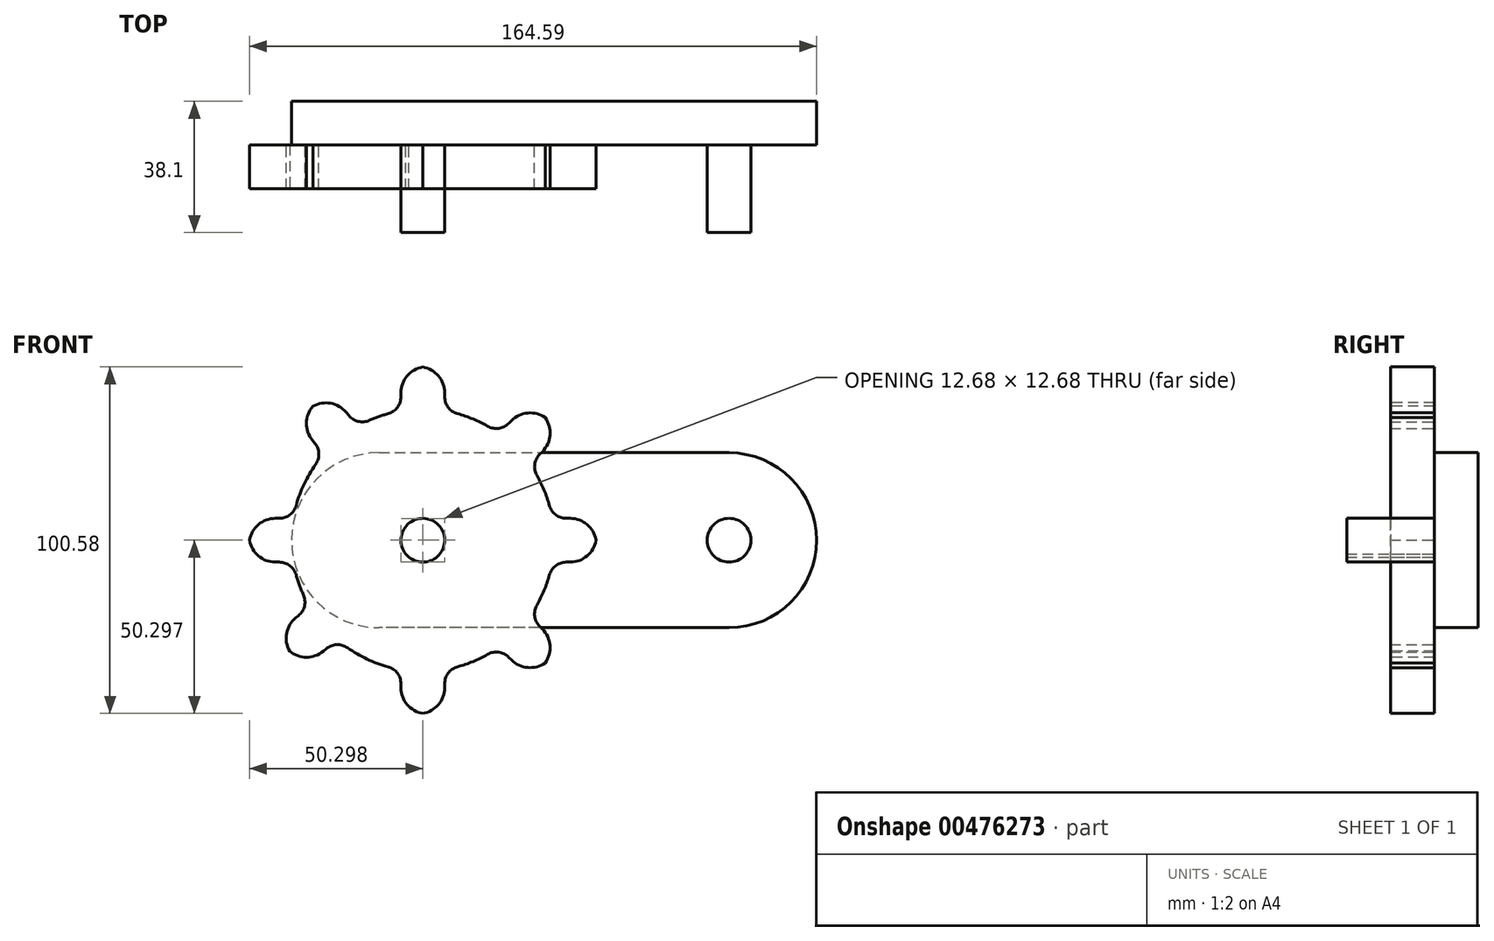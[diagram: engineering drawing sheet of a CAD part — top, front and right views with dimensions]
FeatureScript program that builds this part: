
annotation { "Feature Type Name" : "Feature", "Feature Type Description" : "" }
export const myFeature = defineFeature(function(context is Context, id is Id, definition is map)
    precondition{}
    {
        {
            var Q0;
            Q0=qCreatedBy(makeId("Front.planeOp"),FACE);
            var sketch = newSketch(context, id + "F0", { "sketchPlane" : qUnion([Q0])});
            skLineSegment(sketch, "E0.top", {"start": v(0, 25.4) * mm, "end": v(50.8, 25.4) * mm});
            skLineSegment(sketch, "E0.right", {"start": v(50.8, 0) * mm, "end": v(50.8, 25.4) * mm});
            skLineSegment(sketch, "E1.bottom", {"start": v(50.8, 25.4) * mm, "end": v(-50.8, 25.4) * mm});
            skLineSegment(sketch, "E1.top", {"start": v(50.8, -25.4) * mm, "end": v(-50.8, -25.4) * mm});
            skLineSegment(sketch, "E1.left", {"start": v(50.8, 25.4) * mm, "end": v(50.8, -25.4) * mm});
            skLineSegment(sketch, "E1.right", {"start": v(-50.8, 25.4) * mm, "end": v(-50.8, -25.4) * mm});
            skCircle(sketch, "E2", {"center": v(-50.8, 0) * mm, "radius": 25.4 * mm});
            skCircle(sketch, "E3", {"center": v(50.8, 0) * mm, "radius": 25.4 * mm});
            skSolve(sketch);
        }
        {
            var Q0;
            Q0 = qSketchRegion(id + "F0", true);
            extrude(context, id + "F1", {"entities" : qUnion([Q0]), "depth" : 12.7 * mm});
        }
        {
            var Q0;
            Q0=makeQuery(id+"F1.opExtrude","CAP_FACE",FACE,{"disambiguationData":[OSD([sQuery(id+"F0.wireOp",EDGE,"E1.bottom"),sQuery(id+"F0.wireOp",EDGE,"E1.top"),sQuery(id+"F0.wireOp",EDGE,"E2"),sQuery(id+"F0.wireOp",EDGE,"E3")])],"isStart":false});
            var sketch = newSketch(context, id + "F2", { "sketchPlane" : qUnion([Q0])});
            skCircle(sketch, "E4", {"center": v(50.8, 0) * mm, "radius": 50.8 * mm, "construction": true});
            skCircle(sketch, "E5", {"center": v(-38.1, 0) * mm, "radius": 38.1 * mm});
            skCircle(sketch, "E6", {"center": v(-38.1, 0) * mm, "radius": 6.35 * mm});
            skCircle(sketch, "E7", {"center": v(50.8, 0) * mm, "radius": 6.35 * mm});
            skCircle(sketch, "E8", {"center": v(-38.1, 0) * mm, "radius": 50.8 * mm, "construction": true});
            skCircle(sketch, "E9", {"center": v(50.8, 0) * mm, "radius": 38.1 * mm, "construction": true});
            skLineSegment(sketch, "E10.bottom", {"start": v(-44.45, 0) * mm, "end": v(-31.75, 0) * mm});
            skLineSegment(sketch, "E10.top", {"start": v(-44.45, -50.4) * mm, "end": v(-31.75, -50.4) * mm});
            skLineSegment(sketch, "E10.left", {"start": v(-44.45, 0) * mm, "end": v(-44.45, -50.4) * mm});
            skLineSegment(sketch, "E10.right", {"start": v(-31.75, 0) * mm, "end": v(-31.75, -50.4) * mm});
            skLineSegment(sketch, "E11.top", {"start": v(-44.45, 50.4) * mm, "end": v(-31.75, 50.4) * mm});
            skLineSegment(sketch, "E11.left", {"start": v(-44.45, 0) * mm, "end": v(-44.45, 50.4) * mm});
            skLineSegment(sketch, "E11.right", {"start": v(-31.75, 0) * mm, "end": v(-31.75, 50.4) * mm});
            skLineSegment(sketch, "E12.bottom", {"start": v(-38.1, 6.35) * mm, "end": v(12.3, 6.35) * mm});
            skLineSegment(sketch, "E12.top", {"start": v(-38.1, -6.35) * mm, "end": v(12.3, -6.35) * mm});
            skLineSegment(sketch, "E12.left", {"start": v(-38.1, 6.35) * mm, "end": v(-38.1, -6.35) * mm});
            skLineSegment(sketch, "E12.right", {"start": v(12.3, 6.35) * mm, "end": v(12.3, -6.35) * mm});
            skLineSegment(sketch, "E13", {"start": v(-6.95, 40.13) * mm, "end": v(-44.45, 2.63) * mm});
            skLineSegment(sketch, "E14", {"start": v(-6.95, 40.13) * mm, "end": v(2.03, 31.15) * mm});
            skLineSegment(sketch, "E15", {"start": v(2.03, 31.15) * mm, "end": v(-31.75, -2.63) * mm});
            skLineSegment(sketch, "E16", {"start": v(-65.16, 43) * mm, "end": v(-74.98, 34.94) * mm});
            skLineSegment(sketch, "E17", {"start": v(-74.98, 34.94) * mm, "end": v(-43, -4.03) * mm});
            skPoint(sketch, "E18.endSnap0", {"position": v(0, -25.4) * mm});
            skLineSegment(sketch, "E19", {"start": v(-65.16, 43) * mm, "end": v(-31.75, 2.27) * mm});
            skLineSegment(sketch, "E20", {"start": v(-38.1, 6.35) * mm, "end": v(-88.5, 6.35) * mm});
            skLineSegment(sketch, "E21", {"start": v(-88.5, 6.35) * mm, "end": v(-88.5, -6.35) * mm});
            skLineSegment(sketch, "E22", {"start": v(-88.5, -6.35) * mm, "end": v(-38.1, -6.35) * mm});
            skLineSegment(sketch, "E23", {"start": v(-72.82, -37.08) * mm, "end": v(-80.94, -27.3) * mm});
            skLineSegment(sketch, "E24", {"start": v(-72.82, -37.08) * mm, "end": v(-34.04, -4.89) * mm});
            skLineSegment(sketch, "E25", {"start": v(-80.94, -27.3) * mm, "end": v(-43.88, 2.63) * mm});
            skLineSegment(sketch, "E26", {"start": v(-6.98, -40.15) * mm, "end": v(2.01, -31.17) * mm});
            skLineSegment(sketch, "E27", {"start": v(-33.2, 4.03) * mm, "end": v(2.01, -31.17) * mm});
            skLineSegment(sketch, "E28", {"start": v(-6.98, -40.15) * mm, "end": v(-43, -4.03) * mm});
            skSolve(sketch);
        }
        {
            var Q0;
            {var subQ1=sQuery(id+"F2.wireOp",EDGE,"E6");var subQ3=makeQuery(id+"F2.imprint","INTERSECT",VERTEX,{"derivedFrom":[subQ1,sQuery(id+"F2.wireOp",EDGE,"E13")]});Q0=makeQuery(id+"F2.imprint","IMPRINT",FACE,{"disambiguationData":[TD([[makeQuery(id+"F2.imprint","IMPRINT",EDGE,{"disambiguationData":[TD([[subQ3,1.0]])],"derivedFrom":subQ1}),1.0]])]});}
            var Q1;
            {var subQ1=sQuery(id+"F2.wireOp",EDGE,"E6");var subQ3=makeQuery(id+"F2.imprint","INTERSECT",VERTEX,{"derivedFrom":[subQ1,sQuery(id+"F2.wireOp",EDGE,"E19")]});Q1=makeQuery(id+"F2.imprint","IMPRINT",FACE,{"disambiguationData":[TD([[makeQuery(id+"F2.imprint","IMPRINT",EDGE,{"disambiguationData":[TD([[subQ3,1.0]])],"derivedFrom":subQ1}),1.0]])]});}
            var Q2;
            {var subQ1=sQuery(id+"F2.wireOp",EDGE,"E6");var subQ5=sQuery(id+"F2.wireOp",EDGE,"LzmBPBVv-P9NO-bYiu-9SXB-eBMxNvQNguUM");var subQ6=makeQuery(id+"F2.imprint","INTERSECT",VERTEX,{"disambiguationData":[OD(0.0)],"derivedFrom":[subQ1,subQ5]});Q2=makeQuery(id+"F2.imprint","IMPRINT",FACE,{"disambiguationData":[TD([[makeQuery(id+"F2.imprint","IMPRINT",EDGE,{"disambiguationData":[TD([[subQ6,-1.0]])],"derivedFrom":subQ5}),1.0]])]});}
            var Q3;
            {var subQ1=sQuery(id+"F2.wireOp",EDGE,"E6");var subQ3=makeQuery(id+"F2.imprint","INTERSECT",VERTEX,{"derivedFrom":[subQ1,sQuery(id+"F2.wireOp",EDGE,"Yprd0iWj-599Q-bIJh-nxla-EBqFV5V5Is4s")]});Q3=makeQuery(id+"F2.imprint","IMPRINT",FACE,{"disambiguationData":[TD([[makeQuery(id+"F2.imprint","IMPRINT",EDGE,{"disambiguationData":[TD([[subQ3,1.0]])],"derivedFrom":subQ1}),1.0]])]});}
            var Q4;
            {var subQ1=sQuery(id+"F2.wireOp",EDGE,"E6");var subQ3=makeQuery(id+"F2.imprint","INTERSECT",VERTEX,{"derivedFrom":[subQ1,sQuery(id+"F2.wireOp",EDGE,"E24")]});Q4=makeQuery(id+"F2.imprint","IMPRINT",FACE,{"disambiguationData":[TD([[makeQuery(id+"F2.imprint","IMPRINT",EDGE,{"disambiguationData":[TD([[subQ3,1.0]])],"derivedFrom":subQ1}),1.0]])]});}
            var Q5;
            {var subQ1=sQuery(id+"F2.wireOp",EDGE,"E6");var subQ6=sQuery(id+"F2.wireOp",EDGE,"E28");var subQ7=makeQuery(id+"F2.imprint","INTERSECT",VERTEX,{"derivedFrom":[subQ1,subQ6]});Q5=makeQuery(id+"F2.imprint","IMPRINT",FACE,{"disambiguationData":[TD([[makeQuery(id+"F2.imprint","IMPRINT",EDGE,{"disambiguationData":[TD([[subQ7,-1.0]])],"derivedFrom":subQ6}),-1.0]])]});}
            extrude(context, id + "F3", {"entities" : qUnion([Q0, Q1, Q2, Q3, Q4, Q5]), "operationType" : NewBodyOperationType.ADD, "depth" : 25.4 * mm});
        }
        {
            var Q0;
            {var subQ5=sQuery(id+"F2.wireOp",EDGE,"E11.top");Q0=makeQuery(id+"F2.imprint","IMPRINT",FACE,{"disambiguationData":[TD([[makeQuery(id+"F2.imprint","IMPRINT",EDGE,{"derivedFrom":subQ5}),-1.0]])]});}
            var Q1;
            {var subQ0=sQuery(id+"F2.wireOp",EDGE,"E13");var subQ1=sQuery(id+"F2.wireOp",EDGE,"E5");var subQ2=makeQuery(id+"F2.imprint","INTERSECT",VERTEX,{"derivedFrom":[subQ1,subQ0]});Q1=makeQuery(id+"F2.imprint","IMPRINT",FACE,{"disambiguationData":[TD([[makeQuery(id+"F2.imprint","IMPRINT",EDGE,{"disambiguationData":[TD([[subQ2,-1.0]])],"derivedFrom":subQ1}),1.0]])]});}
            var Q2;
            {var subQ0=sQuery(id+"F2.wireOp",EDGE,"E20");var subQ1=sQuery(id+"F2.wireOp",EDGE,"E11.left");var subQ2=makeQuery(id+"F2.imprint","INTERSECT",VERTEX,{"derivedFrom":[subQ1,subQ0]});Q2=makeQuery(id+"F2.imprint","IMPRINT",FACE,{"disambiguationData":[TD([[makeQuery(id+"F2.imprint","IMPRINT",EDGE,{"disambiguationData":[TD([[subQ2,-1.0]])],"derivedFrom":subQ1}),-1.0]])]});}
            var Q3;
            {var subQ0=sQuery(id+"F2.wireOp",EDGE,"E19");var subQ1=sQuery(id+"F2.wireOp",EDGE,"E11.left");var subQ2=makeQuery(id+"F2.imprint","INTERSECT",VERTEX,{"derivedFrom":[subQ1,subQ0]});Q3=makeQuery(id+"F2.imprint","IMPRINT",FACE,{"disambiguationData":[TD([[makeQuery(id+"F2.imprint","IMPRINT",EDGE,{"disambiguationData":[TD([[subQ2,-1.0]])],"derivedFrom":subQ1}),1.0]])]});}
            var Q4;
            {var subQ5=sQuery(id+"F2.wireOp",EDGE,"E11.left");var subQ6=makeQuery(id+"F2.imprint","INTERSECT",VERTEX,{"derivedFrom":[subQ5,sQuery(id+"F2.wireOp",EDGE,"E13")]});Q4=makeQuery(id+"F2.imprint","IMPRINT",FACE,{"disambiguationData":[TD([[makeQuery(id+"F2.imprint","IMPRINT",EDGE,{"disambiguationData":[TD([[subQ6,1.0]])],"derivedFrom":subQ5}),1.0]])]});}
            var Q5;
            {var subQ0=sQuery(id+"F2.wireOp",EDGE,"E20");var subQ1=sQuery(id+"F2.wireOp",EDGE,"E17");var subQ2=makeQuery(id+"F2.imprint","INTERSECT",VERTEX,{"derivedFrom":[subQ1,subQ0]});Q5=makeQuery(id+"F2.imprint","IMPRINT",FACE,{"disambiguationData":[TD([[makeQuery(id+"F2.imprint","IMPRINT",EDGE,{"disambiguationData":[TD([[subQ2,1.0]])],"derivedFrom":subQ1}),-1.0]])]});}
            var Q6;
            {var subQ0=sQuery(id+"F2.wireOp",EDGE,"E12.bottom");var subQ1=sQuery(id+"F2.wireOp",EDGE,"E11.right");var subQ2=makeQuery(id+"F2.imprint","INTERSECT",VERTEX,{"derivedFrom":[subQ1,subQ0]});Q6=makeQuery(id+"F2.imprint","IMPRINT",FACE,{"disambiguationData":[TD([[makeQuery(id+"F2.imprint","IMPRINT",EDGE,{"disambiguationData":[TD([[subQ2,-1.0]])],"derivedFrom":subQ1}),1.0]])]});}
            var Q7;
            {var subQ5=sQuery(id+"F2.wireOp",EDGE,"E24");var subQ6=sQuery(id+"F2.wireOp",EDGE,"E5");var subQ7=makeQuery(id+"F2.imprint","INTERSECT",VERTEX,{"derivedFrom":[subQ6,subQ5]});Q7=makeQuery(id+"F2.imprint","IMPRINT",FACE,{"disambiguationData":[TD([[makeQuery(id+"F2.imprint","IMPRINT",EDGE,{"disambiguationData":[TD([[subQ7,-1.0]])],"derivedFrom":subQ6}),1.0]])]});}
            var Q8;
            {var subQ5=sQuery(id+"F2.wireOp",EDGE,"E17");var subQ7=sQuery(id+"F2.wireOp",EDGE,"E20");var subQ8=makeQuery(id+"F2.imprint","INTERSECT",VERTEX,{"derivedFrom":[subQ5,subQ7]});Q8=makeQuery(id+"F2.imprint","IMPRINT",FACE,{"disambiguationData":[TD([[makeQuery(id+"F2.imprint","IMPRINT",EDGE,{"disambiguationData":[TD([[subQ8,-1.0]])],"derivedFrom":subQ5}),-1.0]])]});}
            var Q9;
            {var subQ0=sQuery(id+"F2.wireOp",EDGE,"E10.right");var subQ1=sQuery(id+"F2.wireOp",EDGE,"E5");var subQ2=makeQuery(id+"F2.imprint","INTERSECT",VERTEX,{"derivedFrom":[subQ1,subQ0]});Q9=makeQuery(id+"F2.imprint","IMPRINT",FACE,{"disambiguationData":[TD([[makeQuery(id+"F2.imprint","IMPRINT",EDGE,{"disambiguationData":[TD([[subQ2,-1.0]])],"derivedFrom":subQ1}),1.0]])]});}
            var Q10;
            {var subQ0=sQuery(id+"F2.wireOp",EDGE,"E27");var subQ1=sQuery(id+"F2.wireOp",EDGE,"E5");var subQ2=makeQuery(id+"F2.imprint","INTERSECT",VERTEX,{"derivedFrom":[subQ1,subQ0]});Q10=makeQuery(id+"F2.imprint","IMPRINT",FACE,{"disambiguationData":[TD([[makeQuery(id+"F2.imprint","IMPRINT",EDGE,{"disambiguationData":[TD([[subQ2,1.0]])],"derivedFrom":subQ1}),-1.0]])]});}
            var Q11;
            {var subQ1=sQuery(id+"F2.wireOp",EDGE,"E14");Q11=makeQuery(id+"F2.imprint","IMPRINT",FACE,{"disambiguationData":[TD([[makeQuery(id+"F2.imprint","IMPRINT",EDGE,{"derivedFrom":subQ1}),-1.0]])]});}
            var Q12;
            {var subQ0=sQuery(id+"F2.wireOp",EDGE,"E13");var subQ1=sQuery(id+"F2.wireOp",EDGE,"E5");var subQ2=makeQuery(id+"F2.imprint","INTERSECT",VERTEX,{"derivedFrom":[subQ1,subQ0]});Q12=makeQuery(id+"F2.imprint","IMPRINT",FACE,{"disambiguationData":[TD([[makeQuery(id+"F2.imprint","IMPRINT",EDGE,{"disambiguationData":[TD([[subQ2,1.0]])],"derivedFrom":subQ1}),1.0]])]});}
            var Q13;
            {var subQ0=sQuery(id+"F2.wireOp",EDGE,"E22");var subQ1=sQuery(id+"F2.wireOp",EDGE,"E10.left");var subQ2=makeQuery(id+"F2.imprint","INTERSECT",VERTEX,{"derivedFrom":[subQ1,subQ0]});Q13=makeQuery(id+"F2.imprint","IMPRINT",FACE,{"disambiguationData":[TD([[makeQuery(id+"F2.imprint","IMPRINT",EDGE,{"disambiguationData":[TD([[subQ2,-1.0]])],"derivedFrom":subQ1}),1.0]])]});}
            var Q14;
            {var subQ0=sQuery(id+"F2.wireOp",EDGE,"E22");var subQ1=sQuery(id+"F2.wireOp",EDGE,"E5");var subQ2=makeQuery(id+"F2.imprint","INTERSECT",VERTEX,{"derivedFrom":[subQ1,subQ0]});Q14=makeQuery(id+"F2.imprint","IMPRINT",FACE,{"disambiguationData":[TD([[makeQuery(id+"F2.imprint","IMPRINT",EDGE,{"disambiguationData":[TD([[subQ2,-1.0]])],"derivedFrom":subQ1}),1.0]])]});}
            var Q15;
            {var subQ1=sQuery(id+"F2.wireOp",EDGE,"E22");var subQ6=sQuery(id+"F2.wireOp",EDGE,"E10.left");var subQ9=makeQuery(id+"F2.imprint","INTERSECT",VERTEX,{"derivedFrom":[subQ6,subQ1]});Q15=makeQuery(id+"F2.imprint","IMPRINT",FACE,{"disambiguationData":[TD([[makeQuery(id+"F2.imprint","IMPRINT",EDGE,{"disambiguationData":[TD([[subQ9,-1.0]])],"derivedFrom":subQ6}),-1.0]])]});}
            var Q16;
            {var subQ0=sQuery(id+"F2.wireOp",EDGE,"E27");var subQ1=sQuery(id+"F2.wireOp",EDGE,"E5");var subQ2=makeQuery(id+"F2.imprint","INTERSECT",VERTEX,{"derivedFrom":[subQ1,subQ0]});Q16=makeQuery(id+"F2.imprint","IMPRINT",FACE,{"disambiguationData":[TD([[makeQuery(id+"F2.imprint","IMPRINT",EDGE,{"disambiguationData":[TD([[subQ2,1.0]])],"derivedFrom":subQ1}),1.0]])]});}
            var Q17;
            {var subQ0=sQuery(id+"F2.wireOp",EDGE,"E21");Q17=makeQuery(id+"F2.imprint","IMPRINT",FACE,{"disambiguationData":[TD([[makeQuery(id+"F2.imprint","IMPRINT",EDGE,{"derivedFrom":subQ0}),1.0]])]});}
            var Q18;
            {var subQ5=sQuery(id+"F2.wireOp",EDGE,"E12.right");Q18=makeQuery(id+"F2.imprint","IMPRINT",FACE,{"disambiguationData":[TD([[makeQuery(id+"F2.imprint","IMPRINT",EDGE,{"derivedFrom":subQ5}),-1.0]])]});}
            var Q19;
            {var subQ1=sQuery(id+"F2.wireOp",EDGE,"E12.bottom");var subQ5=sQuery(id+"F2.wireOp",EDGE,"E5");var subQ6=makeQuery(id+"F2.imprint","INTERSECT",VERTEX,{"derivedFrom":[subQ5,subQ1]});Q19=makeQuery(id+"F2.imprint","IMPRINT",FACE,{"disambiguationData":[TD([[makeQuery(id+"F2.imprint","IMPRINT",EDGE,{"disambiguationData":[TD([[subQ6,1.0]])],"derivedFrom":subQ5}),1.0]])]});}
            var Q20;
            {var subQ0=sQuery(id+"F2.wireOp",EDGE,"E17");var subQ1=sQuery(id+"F2.wireOp",EDGE,"E10.left");var subQ2=makeQuery(id+"F2.imprint","INTERSECT",VERTEX,{"derivedFrom":[subQ1,subQ0]});Q20=makeQuery(id+"F2.imprint","IMPRINT",FACE,{"disambiguationData":[TD([[makeQuery(id+"F2.imprint","IMPRINT",EDGE,{"disambiguationData":[TD([[subQ2,-1.0]])],"derivedFrom":subQ1}),-1.0]])]});}
            var Q21;
            {var subQ3=sQuery(id+"F2.wireOp",EDGE,"E24");var subQ5=sQuery(id+"F2.wireOp",EDGE,"E10.left");var subQ6=makeQuery(id+"F2.imprint","INTERSECT",VERTEX,{"derivedFrom":[subQ5,subQ3]});Q21=makeQuery(id+"F2.imprint","IMPRINT",FACE,{"disambiguationData":[TD([[makeQuery(id+"F2.imprint","IMPRINT",EDGE,{"disambiguationData":[TD([[subQ6,-1.0]])],"derivedFrom":subQ5}),1.0]])]});}
            var Q22;
            {var subQ0=sQuery(id+"F2.wireOp",EDGE,"E27");var subQ1=sQuery(id+"F2.wireOp",EDGE,"E11.right");var subQ2=makeQuery(id+"F2.imprint","INTERSECT",VERTEX,{"derivedFrom":[subQ1,subQ0]});Q22=makeQuery(id+"F2.imprint","IMPRINT",FACE,{"disambiguationData":[TD([[makeQuery(id+"F2.imprint","IMPRINT",EDGE,{"disambiguationData":[TD([[subQ2,-1.0]])],"derivedFrom":subQ1}),-1.0]])]});}
            var Q23;
            {var subQ0=sQuery(id+"F2.wireOp",EDGE,"E11.left");var subQ1=sQuery(id+"F2.wireOp",EDGE,"E5");var subQ2=makeQuery(id+"F2.imprint","INTERSECT",VERTEX,{"derivedFrom":[subQ1,subQ0]});Q23=makeQuery(id+"F2.imprint","IMPRINT",FACE,{"disambiguationData":[TD([[makeQuery(id+"F2.imprint","IMPRINT",EDGE,{"disambiguationData":[TD([[subQ2,-1.0]])],"derivedFrom":subQ1}),1.0]])]});}
            var Q24;
            {var subQ0=sQuery(id+"F2.wireOp",EDGE,"E25");var subQ1=sQuery(id+"F2.wireOp",EDGE,"E5");var subQ2=makeQuery(id+"F2.imprint","INTERSECT",VERTEX,{"derivedFrom":[subQ1,subQ0]});Q24=makeQuery(id+"F2.imprint","IMPRINT",FACE,{"disambiguationData":[TD([[makeQuery(id+"F2.imprint","IMPRINT",EDGE,{"disambiguationData":[TD([[subQ2,-1.0]])],"derivedFrom":subQ1}),1.0]])]});}
            var Q25;
            {var subQ3=sQuery(id+"F2.wireOp",EDGE,"E19");var subQ5=sQuery(id+"F2.wireOp",EDGE,"E5");var subQ6=makeQuery(id+"F2.imprint","INTERSECT",VERTEX,{"derivedFrom":[subQ5,subQ3]});Q25=makeQuery(id+"F2.imprint","IMPRINT",FACE,{"disambiguationData":[TD([[makeQuery(id+"F2.imprint","IMPRINT",EDGE,{"disambiguationData":[TD([[subQ6,-1.0]])],"derivedFrom":subQ5}),1.0]])]});}
            var Q26;
            {var subQ0=sQuery(id+"F2.wireOp",EDGE,"E19");var subQ1=sQuery(id+"F2.wireOp",EDGE,"E11.left");var subQ2=makeQuery(id+"F2.imprint","INTERSECT",VERTEX,{"derivedFrom":[subQ1,subQ0]});Q26=makeQuery(id+"F2.imprint","IMPRINT",FACE,{"disambiguationData":[TD([[makeQuery(id+"F2.imprint","IMPRINT",EDGE,{"disambiguationData":[TD([[subQ2,-1.0]])],"derivedFrom":subQ1}),-1.0]])]});}
            var Q27;
            {var subQ0=sQuery(id+"F2.wireOp",EDGE,"E28");var subQ1=sQuery(id+"F2.wireOp",EDGE,"E5");var subQ2=makeQuery(id+"F2.imprint","INTERSECT",VERTEX,{"derivedFrom":[subQ1,subQ0]});Q27=makeQuery(id+"F2.imprint","IMPRINT",FACE,{"disambiguationData":[TD([[makeQuery(id+"F2.imprint","IMPRINT",EDGE,{"disambiguationData":[TD([[subQ2,-1.0]])],"derivedFrom":subQ1}),1.0]])]});}
            var Q28;
            {var subQ0=sQuery(id+"F2.wireOp",EDGE,"E15");var subQ1=sQuery(id+"F2.wireOp",EDGE,"E10.right");var subQ2=makeQuery(id+"F2.imprint","INTERSECT",VERTEX,{"derivedFrom":[subQ1,subQ0]});Q28=makeQuery(id+"F2.imprint","IMPRINT",FACE,{"disambiguationData":[TD([[makeQuery(id+"F2.imprint","IMPRINT",EDGE,{"disambiguationData":[TD([[subQ2,-1.0]])],"derivedFrom":subQ1}),1.0]])]});}
            var Q29;
            {var subQ0=sQuery(id+"F2.wireOp",EDGE,"E10.left");var subQ1=sQuery(id+"F2.wireOp",EDGE,"E5");var subQ2=makeQuery(id+"F2.imprint","INTERSECT",VERTEX,{"derivedFrom":[subQ1,subQ0]});Q29=makeQuery(id+"F2.imprint","IMPRINT",FACE,{"disambiguationData":[TD([[makeQuery(id+"F2.imprint","IMPRINT",EDGE,{"disambiguationData":[TD([[subQ2,-1.0]])],"derivedFrom":subQ1}),1.0]])]});}
            var Q30;
            {var subQ0=sQuery(id+"F2.wireOp",EDGE,"E17");var subQ1=sQuery(id+"F2.wireOp",EDGE,"E5");var subQ2=makeQuery(id+"F2.imprint","INTERSECT",VERTEX,{"derivedFrom":[subQ1,subQ0]});Q30=makeQuery(id+"F2.imprint","IMPRINT",FACE,{"disambiguationData":[TD([[makeQuery(id+"F2.imprint","IMPRINT",EDGE,{"disambiguationData":[TD([[subQ2,-1.0]])],"derivedFrom":subQ1}),1.0]])]});}
            var Q31;
            {var subQ0=sQuery(id+"F2.wireOp",EDGE,"E12.top");var subQ1=sQuery(id+"F2.wireOp",EDGE,"E10.right");var subQ2=makeQuery(id+"F2.imprint","INTERSECT",VERTEX,{"derivedFrom":[subQ1,subQ0]});Q31=makeQuery(id+"F2.imprint","IMPRINT",FACE,{"disambiguationData":[TD([[makeQuery(id+"F2.imprint","IMPRINT",EDGE,{"disambiguationData":[TD([[subQ2,-1.0]])],"derivedFrom":subQ1}),-1.0]])]});}
            var Q32;
            {var subQ0=sQuery(id+"F2.wireOp",EDGE,"E13");var subQ1=sQuery(id+"F2.wireOp",EDGE,"E11.right");var subQ2=makeQuery(id+"F2.imprint","INTERSECT",VERTEX,{"derivedFrom":[subQ1,subQ0]});Q32=makeQuery(id+"F2.imprint","IMPRINT",FACE,{"disambiguationData":[TD([[makeQuery(id+"F2.imprint","IMPRINT",EDGE,{"disambiguationData":[TD([[subQ2,-1.0]])],"derivedFrom":subQ1}),-1.0]])]});}
            var Q33;
            {var subQ0=sQuery(id+"F2.wireOp",EDGE,"E28");var subQ1=sQuery(id+"F2.wireOp",EDGE,"E10.right");var subQ2=makeQuery(id+"F2.imprint","INTERSECT",VERTEX,{"derivedFrom":[subQ1,subQ0]});Q33=makeQuery(id+"F2.imprint","IMPRINT",FACE,{"disambiguationData":[TD([[makeQuery(id+"F2.imprint","IMPRINT",EDGE,{"disambiguationData":[TD([[subQ2,-1.0]])],"derivedFrom":subQ1}),1.0]])]});}
            var Q34;
            {var subQ0=sQuery(id+"F2.wireOp",EDGE,"E15");var subQ1=sQuery(id+"F2.wireOp",EDGE,"E5");var subQ2=makeQuery(id+"F2.imprint","INTERSECT",VERTEX,{"derivedFrom":[subQ1,subQ0]});Q34=makeQuery(id+"F2.imprint","IMPRINT",FACE,{"disambiguationData":[TD([[makeQuery(id+"F2.imprint","IMPRINT",EDGE,{"disambiguationData":[TD([[subQ2,-1.0]])],"derivedFrom":subQ1}),-1.0]])]});}
            var Q35;
            {var subQ0=sQuery(id+"F2.wireOp",EDGE,"E20");var subQ1=sQuery(id+"F2.wireOp",EDGE,"E11.left");var subQ2=makeQuery(id+"F2.imprint","INTERSECT",VERTEX,{"derivedFrom":[subQ1,subQ0]});Q35=makeQuery(id+"F2.imprint","IMPRINT",FACE,{"disambiguationData":[TD([[makeQuery(id+"F2.imprint","IMPRINT",EDGE,{"disambiguationData":[TD([[subQ2,-1.0]])],"derivedFrom":subQ1}),1.0]])]});}
            var Q36;
            {var subQ5=sQuery(id+"F2.wireOp",EDGE,"E16");Q36=makeQuery(id+"F2.imprint","IMPRINT",FACE,{"disambiguationData":[TD([[makeQuery(id+"F2.imprint","IMPRINT",EDGE,{"derivedFrom":subQ5}),1.0]])]});}
            var Q37;
            {var subQ7=sQuery(id+"F2.wireOp",EDGE,"E15");var subQ9=sQuery(id+"F2.wireOp",EDGE,"E5");var subQ10=makeQuery(id+"F2.imprint","INTERSECT",VERTEX,{"derivedFrom":[subQ9,subQ7]});Q37=makeQuery(id+"F2.imprint","IMPRINT",FACE,{"disambiguationData":[TD([[makeQuery(id+"F2.imprint","IMPRINT",EDGE,{"disambiguationData":[TD([[subQ10,-1.0]])],"derivedFrom":subQ9}),1.0]])]});}
            var Q38;
            {var subQ0=sQuery(id+"F2.wireOp",EDGE,"E11.right");var subQ1=sQuery(id+"F2.wireOp",EDGE,"E5");var subQ2=makeQuery(id+"F2.imprint","INTERSECT",VERTEX,{"derivedFrom":[subQ1,subQ0]});Q38=makeQuery(id+"F2.imprint","IMPRINT",FACE,{"disambiguationData":[TD([[makeQuery(id+"F2.imprint","IMPRINT",EDGE,{"disambiguationData":[TD([[subQ2,-1.0]])],"derivedFrom":subQ1}),1.0]])]});}
            var Q39;
            {var subQ0=sQuery(id+"F2.wireOp",EDGE,"E24");var subQ1=sQuery(id+"F2.wireOp",EDGE,"E10.left");var subQ2=makeQuery(id+"F2.imprint","INTERSECT",VERTEX,{"derivedFrom":[subQ1,subQ0]});Q39=makeQuery(id+"F2.imprint","IMPRINT",FACE,{"disambiguationData":[TD([[makeQuery(id+"F2.imprint","IMPRINT",EDGE,{"disambiguationData":[TD([[subQ2,-1.0]])],"derivedFrom":subQ1}),-1.0]])]});}
            var Q40;
            {var subQ1=sQuery(id+"F2.wireOp",EDGE,"E26");Q40=makeQuery(id+"F2.imprint","IMPRINT",FACE,{"disambiguationData":[TD([[makeQuery(id+"F2.imprint","IMPRINT",EDGE,{"derivedFrom":subQ1}),1.0]])]});}
            var Q41;
            {var subQ0=sQuery(id+"F2.wireOp",EDGE,"E25");var subQ1=sQuery(id+"F2.wireOp",EDGE,"E22");var subQ2=makeQuery(id+"F2.imprint","INTERSECT",VERTEX,{"derivedFrom":[subQ1,subQ0]});Q41=makeQuery(id+"F2.imprint","IMPRINT",FACE,{"disambiguationData":[TD([[makeQuery(id+"F2.imprint","IMPRINT",EDGE,{"disambiguationData":[TD([[subQ2,1.0]])],"derivedFrom":subQ1}),-1.0]])]});}
            var Q42;
            {var subQ0=sQuery(id+"F2.wireOp",EDGE,"E15");var subQ1=sQuery(id+"F2.wireOp",EDGE,"E5");var subQ2=makeQuery(id+"F2.imprint","INTERSECT",VERTEX,{"derivedFrom":[subQ1,subQ0]});Q42=makeQuery(id+"F2.imprint","IMPRINT",FACE,{"disambiguationData":[TD([[makeQuery(id+"F2.imprint","IMPRINT",EDGE,{"disambiguationData":[TD([[subQ2,1.0]])],"derivedFrom":subQ1}),1.0]])]});}
            var Q43;
            {var subQ0=sQuery(id+"F2.wireOp",EDGE,"E27");var subQ1=sQuery(id+"F2.wireOp",EDGE,"E5");var subQ2=makeQuery(id+"F2.imprint","INTERSECT",VERTEX,{"derivedFrom":[subQ1,subQ0]});Q43=makeQuery(id+"F2.imprint","IMPRINT",FACE,{"disambiguationData":[TD([[makeQuery(id+"F2.imprint","IMPRINT",EDGE,{"disambiguationData":[TD([[subQ2,-1.0]])],"derivedFrom":subQ1}),1.0]])]});}
            var Q44;
            {var subQ5=sQuery(id+"F2.wireOp",EDGE,"E10.top");Q44=makeQuery(id+"F2.imprint","IMPRINT",FACE,{"disambiguationData":[TD([[makeQuery(id+"F2.imprint","IMPRINT",EDGE,{"derivedFrom":subQ5}),1.0]])]});}
            var Q45;
            {var subQ5=sQuery(id+"F2.wireOp",EDGE,"E23");Q45=makeQuery(id+"F2.imprint","IMPRINT",FACE,{"disambiguationData":[TD([[makeQuery(id+"F2.imprint","IMPRINT",EDGE,{"derivedFrom":subQ5}),-1.0]])]});}
            var Q46;
            {var subQ1=sQuery(id+"F2.wireOp",EDGE,"E10.left");var subQ5=sQuery(id+"F2.wireOp",EDGE,"E17");var subQ8=makeQuery(id+"F2.imprint","INTERSECT",VERTEX,{"derivedFrom":[subQ1,subQ5]});Q46=makeQuery(id+"F2.imprint","IMPRINT",FACE,{"disambiguationData":[TD([[makeQuery(id+"F2.imprint","IMPRINT",EDGE,{"disambiguationData":[TD([[subQ8,-1.0]])],"derivedFrom":subQ1}),1.0]])]});}
            var Q47;
            {var subQ0=sQuery(id+"F2.wireOp",EDGE,"E20");var subQ1=sQuery(id+"F2.wireOp",EDGE,"E5");var subQ2=makeQuery(id+"F2.imprint","INTERSECT",VERTEX,{"derivedFrom":[subQ1,subQ0]});Q47=makeQuery(id+"F2.imprint","IMPRINT",FACE,{"disambiguationData":[TD([[makeQuery(id+"F2.imprint","IMPRINT",EDGE,{"disambiguationData":[TD([[subQ2,-1.0]])],"derivedFrom":subQ1}),1.0]])]});}
            var Q48;
            {var subQ1=sQuery(id+"F2.wireOp",EDGE,"E10.right");var subQ7=makeQuery(id+"F2.imprint","INTERSECT",VERTEX,{"derivedFrom":[subQ1,sQuery(id+"F2.wireOp",EDGE,"E15")]});Q48=makeQuery(id+"F2.imprint","IMPRINT",FACE,{"disambiguationData":[TD([[makeQuery(id+"F2.imprint","IMPRINT",EDGE,{"disambiguationData":[TD([[subQ7,-1.0]])],"derivedFrom":subQ1}),-1.0]])]});}
            var Q49;
            {var subQ0=sQuery(id+"F2.wireOp",EDGE,"E27");var subQ1=sQuery(id+"F2.wireOp",EDGE,"E11.right");var subQ2=makeQuery(id+"F2.imprint","INTERSECT",VERTEX,{"derivedFrom":[subQ1,subQ0]});Q49=makeQuery(id+"F2.imprint","IMPRINT",FACE,{"disambiguationData":[TD([[makeQuery(id+"F2.imprint","IMPRINT",EDGE,{"disambiguationData":[TD([[subQ2,-1.0]])],"derivedFrom":subQ1}),1.0]])]});}
            var Q50;
            {var subQ0=sQuery(id+"F2.wireOp",EDGE,"E25");var subQ1=sQuery(id+"F2.wireOp",EDGE,"E6");var subQ2=makeQuery(id+"F2.imprint","INTERSECT",VERTEX,{"derivedFrom":[subQ1,subQ0]});Q50=makeQuery(id+"F2.imprint","IMPRINT",FACE,{"disambiguationData":[TD([[makeQuery(id+"F2.imprint","IMPRINT",EDGE,{"disambiguationData":[TD([[subQ2,1.0]])],"derivedFrom":subQ1}),-1.0]])]});}
            var Q51;
            {var subQ0=sQuery(id+"F2.wireOp",EDGE,"E13");var subQ1=sQuery(id+"F2.wireOp",EDGE,"E11.left");var subQ2=makeQuery(id+"F2.imprint","INTERSECT",VERTEX,{"derivedFrom":[subQ1,subQ0]});Q51=makeQuery(id+"F2.imprint","IMPRINT",FACE,{"disambiguationData":[TD([[makeQuery(id+"F2.imprint","IMPRINT",EDGE,{"disambiguationData":[TD([[subQ2,-1.0]])],"derivedFrom":subQ1}),-1.0]])]});}
            var Q52;
            {var subQ0=sQuery(id+"F2.wireOp",EDGE,"E12.bottom");var subQ3=sQuery(id+"F2.wireOp",EDGE,"E19");var subQ5=makeQuery(id+"F2.imprint","INTERSECT",VERTEX,{"derivedFrom":[subQ0,subQ3]});Q52=makeQuery(id+"F2.imprint","IMPRINT",FACE,{"disambiguationData":[TD([[makeQuery(id+"F2.imprint","IMPRINT",EDGE,{"disambiguationData":[TD([[subQ5,-1.0]])],"derivedFrom":subQ3}),-1.0]])]});}
            var Q53;
            {var subQ0=sQuery(id+"F2.wireOp",EDGE,"E22");var subQ1=sQuery(id+"F2.wireOp",EDGE,"E5");var subQ2=makeQuery(id+"F2.imprint","INTERSECT",VERTEX,{"derivedFrom":[subQ1,subQ0]});Q53=makeQuery(id+"F2.imprint","IMPRINT",FACE,{"disambiguationData":[TD([[makeQuery(id+"F2.imprint","IMPRINT",EDGE,{"disambiguationData":[TD([[subQ2,1.0]])],"derivedFrom":subQ1}),1.0]])]});}
            var Q54;
            {var subQ3=sQuery(id+"F2.wireOp",EDGE,"E19");var subQ5=sQuery(id+"F2.wireOp",EDGE,"E13");var subQ7=makeQuery(id+"F2.imprint","INTERSECT",VERTEX,{"derivedFrom":[subQ5,subQ3]});Q54=makeQuery(id+"F2.imprint","IMPRINT",FACE,{"disambiguationData":[TD([[makeQuery(id+"F2.imprint","IMPRINT",EDGE,{"disambiguationData":[TD([[subQ7,-1.0]])],"derivedFrom":subQ5}),1.0]])]});}
            var Q55;
            {var subQ5=sQuery(id+"F2.wireOp",EDGE,"E11.right");var subQ6=makeQuery(id+"F2.imprint","INTERSECT",VERTEX,{"derivedFrom":[subQ5,sQuery(id+"F2.wireOp",EDGE,"E19")]});Q55=makeQuery(id+"F2.imprint","IMPRINT",FACE,{"disambiguationData":[TD([[makeQuery(id+"F2.imprint","IMPRINT",EDGE,{"disambiguationData":[TD([[subQ6,-1.0]])],"derivedFrom":subQ5}),-1.0]])]});}
            var Q56;
            {var subQ0=sQuery(id+"F2.wireOp",EDGE,"E19");var subQ1=sQuery(id+"F2.wireOp",EDGE,"E11.right");var subQ2=makeQuery(id+"F2.imprint","INTERSECT",VERTEX,{"derivedFrom":[subQ1,subQ0]});Q56=makeQuery(id+"F2.imprint","IMPRINT",FACE,{"disambiguationData":[TD([[makeQuery(id+"F2.imprint","IMPRINT",EDGE,{"disambiguationData":[TD([[subQ2,-1.0]])],"derivedFrom":subQ1}),1.0]])]});}
            var Q57;
            {var subQ1=sQuery(id+"F2.wireOp",EDGE,"E6");var subQ3=sQuery(id+"F2.wireOp",EDGE,"E13");var subQ4=makeQuery(id+"F2.imprint","INTERSECT",VERTEX,{"derivedFrom":[subQ1,subQ3]});Q57=makeQuery(id+"F2.imprint","IMPRINT",FACE,{"disambiguationData":[TD([[makeQuery(id+"F2.imprint","IMPRINT",EDGE,{"disambiguationData":[TD([[subQ4,1.0]])],"derivedFrom":subQ3}),1.0]])]});}
            var Q58;
            {var subQ1=sQuery(id+"F2.wireOp",EDGE,"E6");var subQ3=sQuery(id+"F2.wireOp",EDGE,"E28");var subQ4=makeQuery(id+"F2.imprint","INTERSECT",VERTEX,{"derivedFrom":[subQ1,subQ3]});Q58=makeQuery(id+"F2.imprint","IMPRINT",FACE,{"disambiguationData":[TD([[makeQuery(id+"F2.imprint","IMPRINT",EDGE,{"disambiguationData":[TD([[subQ4,1.0]])],"derivedFrom":subQ3}),-1.0]])]});}
            var Q59;
            {var subQ1=sQuery(id+"F2.wireOp",EDGE,"E6");var subQ3=sQuery(id+"F2.wireOp",EDGE,"E24");var subQ4=makeQuery(id+"F2.imprint","INTERSECT",VERTEX,{"derivedFrom":[subQ1,subQ3]});Q59=makeQuery(id+"F2.imprint","IMPRINT",FACE,{"disambiguationData":[TD([[makeQuery(id+"F2.imprint","IMPRINT",EDGE,{"disambiguationData":[TD([[subQ4,1.0]])],"derivedFrom":subQ3}),1.0]])]});}
            var Q60;
            {var subQ0=sQuery(id+"F2.wireOp",EDGE,"E10.left");var subQ3=sQuery(id+"F2.wireOp",EDGE,"E17");var subQ5=makeQuery(id+"F2.imprint","INTERSECT",VERTEX,{"derivedFrom":[subQ0,subQ3]});Q60=makeQuery(id+"F2.imprint","IMPRINT",FACE,{"disambiguationData":[TD([[makeQuery(id+"F2.imprint","IMPRINT",EDGE,{"disambiguationData":[TD([[subQ5,-1.0]])],"derivedFrom":subQ3}),1.0]])]});}
            var Q61;
            {var subQ0=sQuery(id+"F2.wireOp",EDGE,"E11.right");var subQ3=sQuery(id+"F2.wireOp",EDGE,"E19");var subQ5=makeQuery(id+"F2.imprint","INTERSECT",VERTEX,{"derivedFrom":[subQ0,subQ3]});Q61=makeQuery(id+"F2.imprint","IMPRINT",FACE,{"disambiguationData":[TD([[makeQuery(id+"F2.imprint","IMPRINT",EDGE,{"disambiguationData":[TD([[subQ5,1.0]])],"derivedFrom":subQ3}),-1.0]])]});}
            var Q62;
            {var subQ0=sQuery(id+"F2.wireOp",EDGE,"E28");var subQ1=sQuery(id+"F2.wireOp",EDGE,"E6");var subQ3=makeQuery(id+"F2.imprint","INTERSECT",VERTEX,{"derivedFrom":[subQ1,subQ0]});Q62=makeQuery(id+"F2.imprint","IMPRINT",FACE,{"disambiguationData":[TD([[makeQuery(id+"F2.imprint","IMPRINT",EDGE,{"disambiguationData":[TD([[subQ3,1.0]])],"derivedFrom":subQ1}),1.0]])]});}
            var Q63;
            {var subQ1=sQuery(id+"F2.wireOp",EDGE,"E12.top");var subQ3=sQuery(id+"F2.wireOp",EDGE,"E24");var subQ4=makeQuery(id+"F2.imprint","INTERSECT",VERTEX,{"derivedFrom":[subQ1,subQ3]});Q63=makeQuery(id+"F2.imprint","IMPRINT",FACE,{"disambiguationData":[TD([[makeQuery(id+"F2.imprint","IMPRINT",EDGE,{"disambiguationData":[TD([[subQ4,1.0]])],"derivedFrom":subQ3}),1.0]])]});}
            var Q64;
            {var subQ1=sQuery(id+"F2.wireOp",EDGE,"E10.left");var subQ3=sQuery(id+"F2.wireOp",EDGE,"E17");var subQ4=makeQuery(id+"F2.imprint","INTERSECT",VERTEX,{"derivedFrom":[subQ1,subQ3]});Q64=makeQuery(id+"F2.imprint","IMPRINT",FACE,{"disambiguationData":[TD([[makeQuery(id+"F2.imprint","IMPRINT",EDGE,{"disambiguationData":[TD([[subQ4,1.0]])],"derivedFrom":subQ3}),1.0]])]});}
            var Q65;
            {var subQ1=sQuery(id+"F2.wireOp",EDGE,"E6");var subQ3=sQuery(id+"F2.wireOp",EDGE,"E25");var subQ4=makeQuery(id+"F2.imprint","INTERSECT",VERTEX,{"derivedFrom":[subQ1,subQ3]});Q65=makeQuery(id+"F2.imprint","IMPRINT",FACE,{"disambiguationData":[TD([[makeQuery(id+"F2.imprint","IMPRINT",EDGE,{"disambiguationData":[TD([[subQ4,1.0]])],"derivedFrom":subQ3}),-1.0]])]});}
            extrude(context, id + "F4", {"entities" : qUnion([Q0, Q1, Q2, Q3, Q4, Q5, Q6, Q7, Q8, Q9, Q10, Q11, Q12, Q13, Q14, Q15, Q16, Q17, Q18, Q19, Q20, Q21, Q22, Q23, Q24, Q25, Q26, Q27, Q28, Q29, Q30, Q31, Q32, Q33, Q34, Q35, Q36, Q37, Q38, Q39, Q40, Q41, Q42, Q43, Q44, Q45, Q46, Q47, Q48, Q49, Q50, Q51, Q52, Q53, Q54, Q55, Q56, Q57, Q58, Q59, Q60, Q61, Q62, Q63, Q64, Q65]), "depth" : 12.7 * mm});
        }
        {
            var Q0;
            Q0=makeQuery(id+"F4.opExtrude","SWEPT_EDGE",EDGE,{"disambiguationData":[OSD([sQuery(id+"F2.wireOp",EDGE,"E16"),sQuery(id+"F2.wireOp",EDGE,"E19")])]});
            var Q1;
            Q1=makeQuery(id+"F4.opExtrude","SWEPT_EDGE",EDGE,{"disambiguationData":[OSD([sQuery(id+"F2.wireOp",EDGE,"E16"),sQuery(id+"F2.wireOp",EDGE,"E17")])]});
            var Q2;
            Q2=makeQuery(id+"F4.opExtrude","SWEPT_EDGE",EDGE,{"disambiguationData":[OSD([sQuery(id+"F2.wireOp",EDGE,"E11.top"),sQuery(id+"F2.wireOp",EDGE,"E11.left")])]});
            var Q3;
            Q3=makeQuery(id+"F4.opExtrude","SWEPT_EDGE",EDGE,{"disambiguationData":[OSD([sQuery(id+"F2.wireOp",EDGE,"E11.top"),sQuery(id+"F2.wireOp",EDGE,"E11.right")])]});
            var Q4;
            Q4=makeQuery(id+"F4.opExtrude","SWEPT_EDGE",EDGE,{"disambiguationData":[OSD([sQuery(id+"F2.wireOp",EDGE,"E13"),sQuery(id+"F2.wireOp",EDGE,"E14")])]});
            var Q5;
            Q5=makeQuery(id+"F4.opExtrude","SWEPT_EDGE",EDGE,{"disambiguationData":[OSD([sQuery(id+"F2.wireOp",EDGE,"E14"),sQuery(id+"F2.wireOp",EDGE,"E15")])]});
            var Q6;
            Q6=makeQuery(id+"F4.opExtrude","SWEPT_EDGE",EDGE,{"disambiguationData":[OSD([sQuery(id+"F2.wireOp",EDGE,"E12.bottom"),sQuery(id+"F2.wireOp",EDGE,"E12.right")])]});
            var Q7;
            Q7=makeQuery(id+"F4.opExtrude","SWEPT_EDGE",EDGE,{"disambiguationData":[OSD([sQuery(id+"F2.wireOp",EDGE,"E12.top"),sQuery(id+"F2.wireOp",EDGE,"E12.right")])]});
            var Q8;
            Q8=makeQuery(id+"F4.opExtrude","SWEPT_EDGE",EDGE,{"disambiguationData":[OSD([sQuery(id+"F2.wireOp",EDGE,"E26"),sQuery(id+"F2.wireOp",EDGE,"E28")])]});
            var Q9;
            Q9=makeQuery(id+"F4.opExtrude","SWEPT_EDGE",EDGE,{"disambiguationData":[OSD([sQuery(id+"F2.wireOp",EDGE,"E26"),sQuery(id+"F2.wireOp",EDGE,"E27")])]});
            var Q10;
            Q10=makeQuery(id+"F4.opExtrude","SWEPT_EDGE",EDGE,{"disambiguationData":[OSD([sQuery(id+"F2.wireOp",EDGE,"E10.top"),sQuery(id+"F2.wireOp",EDGE,"E10.right")])]});
            var Q11;
            Q11=makeQuery(id+"F4.opExtrude","SWEPT_EDGE",EDGE,{"disambiguationData":[OSD([sQuery(id+"F2.wireOp",EDGE,"E10.top"),sQuery(id+"F2.wireOp",EDGE,"E10.left")])]});
            var Q12;
            Q12=makeQuery(id+"F4.opExtrude","SWEPT_EDGE",EDGE,{"disambiguationData":[OSD([sQuery(id+"F2.wireOp",EDGE,"E23"),sQuery(id+"F2.wireOp",EDGE,"E24")])]});
            var Q13;
            Q13=makeQuery(id+"F4.opExtrude","SWEPT_EDGE",EDGE,{"disambiguationData":[OSD([sQuery(id+"F2.wireOp",EDGE,"E23"),sQuery(id+"F2.wireOp",EDGE,"E25")])]});
            var Q14;
            Q14=makeQuery(id+"F4.opExtrude","SWEPT_EDGE",EDGE,{"disambiguationData":[OSD([sQuery(id+"F2.wireOp",EDGE,"E21"),sQuery(id+"F2.wireOp",EDGE,"E22")])]});
            var Q15;
            Q15=makeQuery(id+"F4.opExtrude","SWEPT_EDGE",EDGE,{"disambiguationData":[OSD([sQuery(id+"F2.wireOp",EDGE,"E20"),sQuery(id+"F2.wireOp",EDGE,"E21")])]});
            fillet(context, id + "F5", {"entities" : qUnion([Q0, Q1, Q2, Q3, Q4, Q5, Q6, Q7, Q8, Q9, Q10, Q11, Q12, Q13, Q14, Q15]), "radius" : 7.62 * mm, "tangentPropagation" : true, "allowEdgeOverflow" : false});
        }
        {
            var Q0;
            Q0=makeQuery(id+"F2.imprint","IMPRINT",FACE,{"disambiguationData":[TD([[makeQuery(id+"F2.imprint","IMPRINT",EDGE,{"derivedFrom":sQuery(id+"F2.wireOp",EDGE,"E7")}),1.0]])]});
            extrude(context, id + "F6", {"entities" : qUnion([Q0]), "operationType" : NewBodyOperationType.ADD, "depth" : 25.4 * mm});
        }
        {
            var Q0;
            Q0=makeQuery(id+"F4.opExtrude","SWEPT_EDGE",EDGE,{"disambiguationData":[OSD([sQuery(id+"F2.wireOp",EDGE,"E5"),sQuery(id+"F2.wireOp",EDGE,"E11.right")])]});
            var Q1;
            Q1=makeQuery(id+"F4.opExtrude","SWEPT_EDGE",EDGE,{"disambiguationData":[OSD([sQuery(id+"F2.wireOp",EDGE,"E5"),sQuery(id+"F2.wireOp",EDGE,"E13")])]});
            var Q2;
            Q2=makeQuery(id+"F4.opExtrude","SWEPT_EDGE",EDGE,{"disambiguationData":[OSD([sQuery(id+"F2.wireOp",EDGE,"E5"),sQuery(id+"F2.wireOp",EDGE,"E11.left")])]});
            var Q3;
            Q3=makeQuery(id+"F4.opExtrude","SWEPT_EDGE",EDGE,{"disambiguationData":[OSD([sQuery(id+"F2.wireOp",EDGE,"E5"),sQuery(id+"F2.wireOp",EDGE,"E19")])]});
            var Q4;
            Q4=makeQuery(id+"F4.opExtrude","SWEPT_EDGE",EDGE,{"disambiguationData":[OSD([sQuery(id+"F2.wireOp",EDGE,"E5"),sQuery(id+"F2.wireOp",EDGE,"E20")])]});
            var Q5;
            Q5=makeQuery(id+"F4.opExtrude","SWEPT_EDGE",EDGE,{"disambiguationData":[OSD([sQuery(id+"F2.wireOp",EDGE,"E5"),sQuery(id+"F2.wireOp",EDGE,"E17")])]});
            var Q6;
            Q6=makeQuery(id+"F4.opExtrude","SWEPT_EDGE",EDGE,{"disambiguationData":[OSD([sQuery(id+"F2.wireOp",EDGE,"E5"),sQuery(id+"F2.wireOp",EDGE,"E22")])]});
            var Q7;
            Q7=makeQuery(id+"F4.opExtrude","SWEPT_EDGE",EDGE,{"disambiguationData":[OSD([sQuery(id+"F2.wireOp",EDGE,"E5"),sQuery(id+"F2.wireOp",EDGE,"E25")])]});
            var Q8;
            Q8=makeQuery(id+"F4.opExtrude","SWEPT_EDGE",EDGE,{"disambiguationData":[OSD([sQuery(id+"F2.wireOp",EDGE,"E5"),sQuery(id+"F2.wireOp",EDGE,"E24")])]});
            var Q9;
            Q9=makeQuery(id+"F4.opExtrude","SWEPT_EDGE",EDGE,{"disambiguationData":[OSD([sQuery(id+"F2.wireOp",EDGE,"E5"),sQuery(id+"F2.wireOp",EDGE,"E10.left")])]});
            var Q10;
            Q10=makeQuery(id+"F4.opExtrude","SWEPT_EDGE",EDGE,{"disambiguationData":[OSD([sQuery(id+"F2.wireOp",EDGE,"E5"),sQuery(id+"F2.wireOp",EDGE,"E10.right")])]});
            var Q11;
            Q11=makeQuery(id+"F4.opExtrude","SWEPT_EDGE",EDGE,{"disambiguationData":[OSD([sQuery(id+"F2.wireOp",EDGE,"E5"),sQuery(id+"F2.wireOp",EDGE,"E28")])]});
            var Q12;
            Q12=makeQuery(id+"F4.opExtrude","SWEPT_EDGE",EDGE,{"disambiguationData":[OSD([sQuery(id+"F2.wireOp",EDGE,"E5"),sQuery(id+"F2.wireOp",EDGE,"E27")])]});
            var Q13;
            Q13=makeQuery(id+"F4.opExtrude","SWEPT_EDGE",EDGE,{"disambiguationData":[OSD([sQuery(id+"F2.wireOp",EDGE,"E5"),sQuery(id+"F2.wireOp",EDGE,"E15")])]});
            var Q14;
            Q14=makeQuery(id+"F4.opExtrude","SWEPT_EDGE",EDGE,{"disambiguationData":[OSD([sQuery(id+"F2.wireOp",EDGE,"E5"),sQuery(id+"F2.wireOp",EDGE,"E12.bottom")])]});
            var Q15;
            Q15=makeQuery(id+"F4.opExtrude","SWEPT_EDGE",EDGE,{"disambiguationData":[OSD([sQuery(id+"F2.wireOp",EDGE,"E5"),sQuery(id+"F2.wireOp",EDGE,"E12.top")])]});
            fillet(context, id + "F7", {"entities" : qUnion([Q0, Q1, Q2, Q3, Q4, Q5, Q6, Q7, Q8, Q9, Q10, Q11, Q12, Q13, Q14, Q15]), "radius" : 5.08 * mm, "tangentPropagation" : true, "allowEdgeOverflow" : false});
        }
    });
